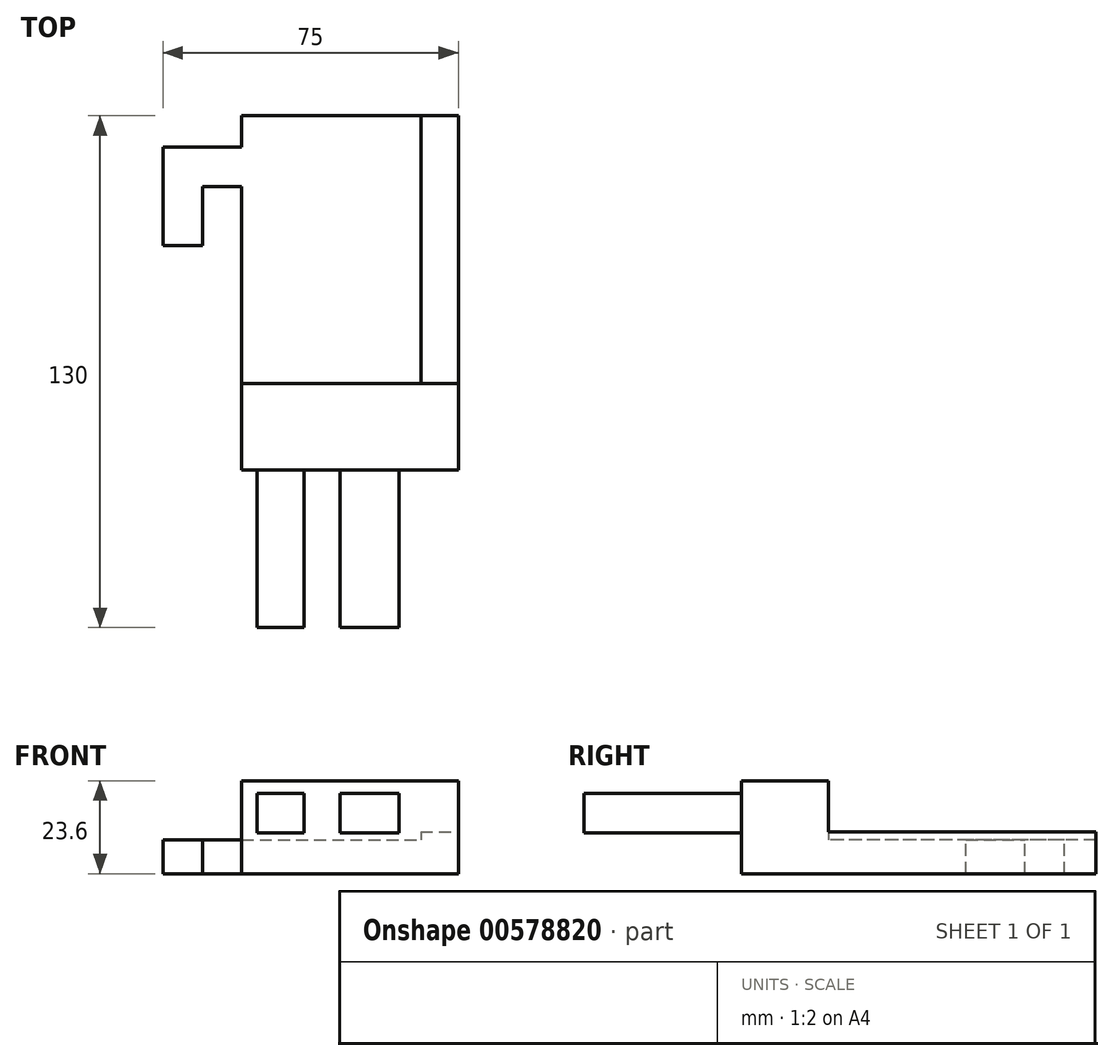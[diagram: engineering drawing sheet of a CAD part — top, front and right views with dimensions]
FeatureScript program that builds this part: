
annotation { "Feature Type Name" : "Feature", "Feature Type Description" : "" }
export const myFeature = defineFeature(function(context is Context, id is Id, definition is map)
    precondition{}
    {
        {
            var Q0;
            Q0=qCreatedBy(makeId("Top.planeOp"),FACE);
            var sketch = newSketch(context, id + "F0", { "sketchPlane" : qUnion([Q0])});
            skLineSegment(sketch, "E0.bottom", {"start": v(-28.93, 51.9) * mm, "end": v(26.07, 51.9) * mm});
            skLineSegment(sketch, "E0.top", {"start": v(-28.93, -38.1) * mm, "end": v(26.07, -38.1) * mm});
            skLineSegment(sketch, "E0.left", {"start": v(-28.93, 51.9) * mm, "end": v(-28.93, -38.1) * mm});
            skLineSegment(sketch, "E0.right", {"start": v(26.07, 51.9) * mm, "end": v(26.07, -38.1) * mm});
            skSolve(sketch);
        }
        {
            var Q0;
            Q0=makeQuery(id+"F0.imprint","IMPRINT",FACE,{"disambiguationData":[TD([[makeQuery(id+"F0.imprint","IMPRINT",EDGE,{"derivedFrom":sQuery(id+"F0.wireOp",EDGE,"E0.bottom")}),-1.0]])]});
            extrude(context, id + "F1", {"entities" : qUnion([Q0]), "depth" : 1.6 * mm, "offsetDistance" : 25 * mm});
        }
        {
            var Q0;
            Q0=makeQuery(id+"F1.opExtrude","CAP_FACE",FACE,{"disambiguationData":[OSD([sQuery(id+"F0.wireOp",EDGE,"E0.bottom"),sQuery(id+"F0.wireOp",EDGE,"E0.top"),sQuery(id+"F0.wireOp",EDGE,"E0.left"),sQuery(id+"F0.wireOp",EDGE,"E0.right")])],"isStart":false});
            var sketch = newSketch(context, id + "F2", { "sketchPlane" : qUnion([Q0])});
            skLineSegment(sketch, "E1.bottom", {"start": v(-28.93, -16.1) * mm, "end": v(26.07, -16.1) * mm});
            skLineSegment(sketch, "E1.top", {"start": v(-28.93, -38.1) * mm, "end": v(26.07, -38.1) * mm});
            skLineSegment(sketch, "E1.left", {"start": v(-28.93, -16.1) * mm, "end": v(-28.93, -38.1) * mm});
            skLineSegment(sketch, "E1.right", {"start": v(26.07, -16.1) * mm, "end": v(26.07, -38.1) * mm});
            skSolve(sketch);
        }
        {
            var Q0;
            Q0=makeQuery(id+"F2.imprint","IMPRINT",FACE,{"disambiguationData":[TD([[makeQuery(id+"F2.imprint","IMPRINT",EDGE,{"derivedFrom":sQuery(id+"F2.wireOp",EDGE,"E1.bottom")}),-1.0]])]});
            extrude(context, id + "F3", {"entities" : qUnion([Q0]), "operationType" : NewBodyOperationType.ADD, "depth" : 22 * mm, "offsetDistance" : 25 * mm});
        }
        {
            var Q0;
            Q0=makeQuery(id+"F3.boolean.opBoolean","MERGE",FACE,{"derivedFrom":[makeQuery(id+"F1.opExtrude","SWEPT_FACE",FACE,{"disambiguationData":[OSD([sQuery(id+"F0.wireOp",EDGE,"E0.top")])]}),makeQuery(id+"F3.opExtrude","SWEPT_FACE",FACE,{"disambiguationData":[OSD([sQuery(id+"F2.wireOp",EDGE,"E1.top")])]})]});
            var sketch = newSketch(context, id + "F4", { "sketchPlane" : qUnion([Q0])});
            skLineSegment(sketch, "E2.bottom", {"start": v(-3.93, 20.42) * mm, "end": v(11.07, 20.42) * mm});
            skLineSegment(sketch, "E2.top", {"start": v(-3.93, 10.42) * mm, "end": v(11.07, 10.42) * mm});
            skLineSegment(sketch, "E2.left", {"start": v(-3.93, 20.42) * mm, "end": v(-3.93, 10.42) * mm});
            skLineSegment(sketch, "E2.right", {"start": v(11.07, 20.42) * mm, "end": v(11.07, 10.42) * mm});
            skLineSegment(sketch, "E3.bottom", {"start": v(-25.07, 20.42) * mm, "end": v(-13.07, 20.42) * mm});
            skLineSegment(sketch, "E3.top", {"start": v(-25.07, 10.42) * mm, "end": v(-13.07, 10.42) * mm});
            skLineSegment(sketch, "E3.left", {"start": v(-25.07, 20.42) * mm, "end": v(-25.07, 10.42) * mm});
            skLineSegment(sketch, "E3.right", {"start": v(-13.07, 20.42) * mm, "end": v(-13.07, 10.42) * mm});
            skSolve(sketch);
        }
        {
            var Q0;
            Q0 = qSketchRegion(id + "F4", true);
            extrude(context, id + "F5", {"entities" : qUnion([Q0]), "operationType" : NewBodyOperationType.ADD, "depth" : 40 * mm, "offsetDistance" : 25 * mm});
        }
        {
            var Q0;
            Q0=makeQuery(id+"F1.opExtrude","CAP_FACE",FACE,{"disambiguationData":[OSD([sQuery(id+"F0.wireOp",EDGE,"E0.bottom"),sQuery(id+"F0.wireOp",EDGE,"E0.top"),sQuery(id+"F0.wireOp",EDGE,"E0.left"),sQuery(id+"F0.wireOp",EDGE,"E0.right")])],"isStart":false});
            extrude(context, id + "F6", {"entities" : qUnion([Q0]), "operationType" : NewBodyOperationType.ADD, "depth" : 7 * mm, "offsetDistance" : 25 * mm});
        }
        {
            var Q0;
            Q0=makeQuery(id+"F6.opExtrude","CAP_FACE",FACE,{"disambiguationData":[OSD([sQuery(id+"F0.wireOp",EDGE,"E0.bottom"),sQuery(id+"F0.wireOp",EDGE,"E0.top"),sQuery(id+"F0.wireOp",EDGE,"E0.left"),sQuery(id+"F0.wireOp",EDGE,"E0.right")])],"isStart":false});
            var sketch = newSketch(context, id + "F7", { "sketchPlane" : qUnion([Q0])});
            skLineSegment(sketch, "E4.bottom", {"start": v(26.07, 51.9) * mm, "end": v(16.58, 51.9) * mm});
            skLineSegment(sketch, "E4.top", {"start": v(26.07, -16.1) * mm, "end": v(16.58, -16.1) * mm});
            skLineSegment(sketch, "E4.left", {"start": v(26.07, 51.9) * mm, "end": v(26.07, -16.1) * mm});
            skLineSegment(sketch, "E4.right", {"start": v(16.58, 51.9) * mm, "end": v(16.58, -16.1) * mm});
            skSolve(sketch);
        }
        {
            var Q0;
            Q0=makeQuery(id+"F7.imprint","IMPRINT",FACE,{"disambiguationData":[TD([[makeQuery(id+"F7.imprint","IMPRINT",EDGE,{"derivedFrom":sQuery(id+"F7.wireOp",EDGE,"E4.bottom")}),-1.0]])]});
            extrude(context, id + "F8", {"entities" : qUnion([Q0]), "operationType" : NewBodyOperationType.ADD, "depth" : 2 * mm, "offsetDistance" : 25 * mm});
        }
        {
            var Q0;
            {var subQ0=sQuery(id+"F0.wireOp",EDGE,"E0.left");Q0=makeQuery(id+"F6.boolean.opBoolean","MERGE",FACE,{"derivedFrom":[makeQuery(id+"F3.boolean.opBoolean","MERGE",FACE,{"derivedFrom":[makeQuery(id+"F1.opExtrude","SWEPT_FACE",FACE,{"disambiguationData":[OSD([subQ0])]}),makeQuery(id+"F3.opExtrude","SWEPT_FACE",FACE,{"disambiguationData":[OSD([sQuery(id+"F2.wireOp",EDGE,"E1.left")])]})]}),makeQuery(id+"F6.opExtrude","SWEPT_FACE",FACE,{"disambiguationData":[OSD([subQ0])]})]});}
            var sketch = newSketch(context, id + "F9", { "sketchPlane" : qUnion([Q0])});
            skLineSegment(sketch, "E5.bottom", {"start": v(-43.9, 0) * mm, "end": v(-33.9, 0) * mm});
            skLineSegment(sketch, "E5.top", {"start": v(-43.9, 8.6) * mm, "end": v(-33.9, 8.6) * mm});
            skLineSegment(sketch, "E5.left", {"start": v(-43.9, 0) * mm, "end": v(-43.9, 8.6) * mm});
            skLineSegment(sketch, "E5.right", {"start": v(-33.9, 0) * mm, "end": v(-33.9, 8.6) * mm});
            skSolve(sketch);
        }
        {
            var Q0;
            Q0=makeQuery(id+"F9.imprint","IMPRINT",FACE,{"disambiguationData":[TD([[makeQuery(id+"F9.imprint","IMPRINT",EDGE,{"derivedFrom":sQuery(id+"F9.wireOp",EDGE,"E5.bottom")}),1.0]])]});
            extrude(context, id + "F10", {"entities" : qUnion([Q0]), "operationType" : NewBodyOperationType.ADD, "depth" : 20 * mm, "offsetDistance" : 25 * mm});
        }
        {
            var Q0;
            Q0=makeQuery(id+"F10.opExtrude","SWEPT_FACE",FACE,{"disambiguationData":[OSD([sQuery(id+"F9.wireOp",EDGE,"E5.right")])]});
            var sketch = newSketch(context, id + "F11", { "sketchPlane" : qUnion([Q0])});
            skLineSegment(sketch, "E6.bottom", {"start": v(-48.93, 8.6) * mm, "end": v(-38.93, 8.6) * mm});
            skLineSegment(sketch, "E6.top", {"start": v(-48.93, 0) * mm, "end": v(-38.93, 0) * mm});
            skLineSegment(sketch, "E6.left", {"start": v(-48.93, 8.6) * mm, "end": v(-48.93, 0) * mm});
            skLineSegment(sketch, "E6.right", {"start": v(-38.93, 8.6) * mm, "end": v(-38.93, 0) * mm});
            skSolve(sketch);
        }
        {
            var Q0;
            Q0=makeQuery(id+"F11.imprint","IMPRINT",FACE,{"disambiguationData":[TD([[makeQuery(id+"F11.imprint","IMPRINT",EDGE,{"derivedFrom":sQuery(id+"F11.wireOp",EDGE,"E6.bottom")}),-1.0]])]});
            extrude(context, id + "F12", {"entities" : qUnion([Q0]), "operationType" : NewBodyOperationType.ADD, "depth" : 15 * mm, "offsetDistance" : 25 * mm});
        }
    });
